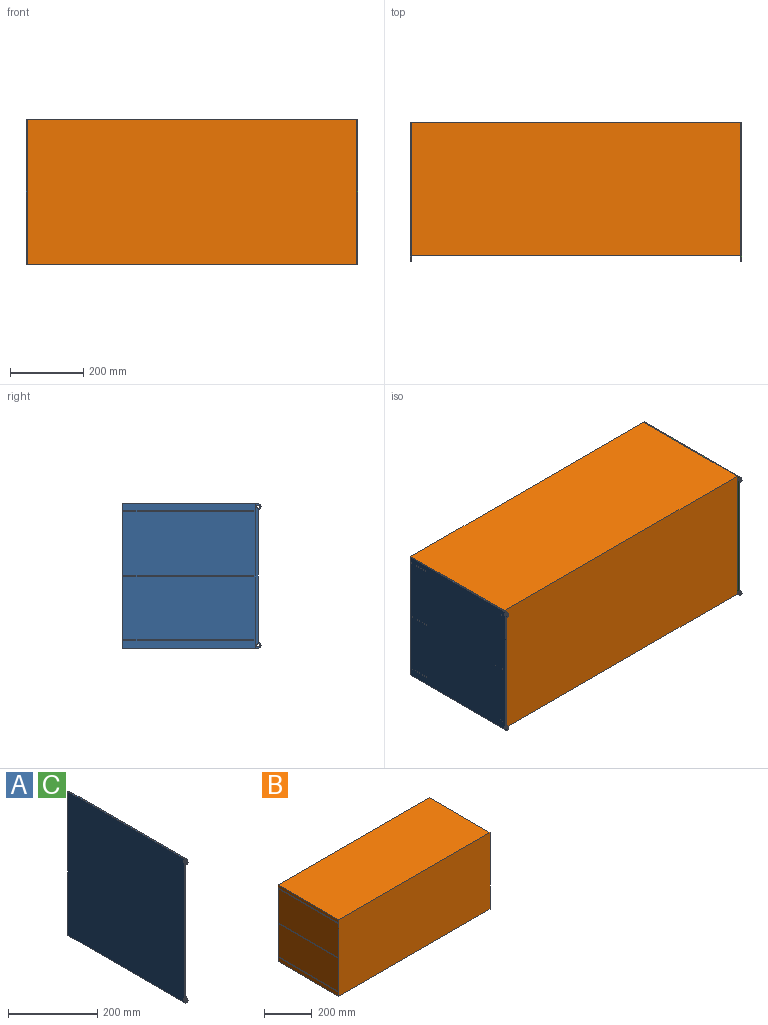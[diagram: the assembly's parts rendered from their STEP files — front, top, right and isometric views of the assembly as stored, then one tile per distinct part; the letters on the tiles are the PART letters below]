
ASSEMBLY  parts=3 mates=2
PART A: 10 faces, bbox 3.2x377.4x394.5 mm
  f0: cylinder r=7.87mm len=15.75mm, axis (-1,0,0), area 78.5mm2, adj f1,f7,f8,f9
  f1: plane 362.99x3.18mm, normal (0,-1,0), area 1152.5mm2, adj f0,f2,f8,f9
  f2: cylinder r=7.87mm len=15.75mm, axis (-1,0,0), area 78.5mm2, adj f1,f3,f8,f9
  f3: plane 369.49x3.18mm, normal (0,0,-1), area 1173.1mm2, adj f2,f4,f8,f9
  f4: plane 394.49x3.18mm, normal (0,1,0), area 1252.5mm2, adj f3,f7,f8,f9
  f5: cylinder r=4mm len=8mm, axis (-1,0,0), area 79.8mm2, adj f8,f9
  f6: cylinder r=4mm len=8mm, axis (-1,0,0), area 79.8mm2, adj f8,f9
  f7: plane 369.49x3.18mm, normal (0,0,1), area 1173.1mm2, adj f0,f4,f8,f9
  f8: plane 394.49x377.37mm, normal (1,0,0), area 145854.9mm2, adj f0,f1,f2,f3,f4,f5,f6,f7
  f9: plane 394.49x377.37mm, normal (-1,0,0), area 145854.9mm2, adj f0,f1,f2,f3,f4,f5,f6,f7
PART B: 50 faces, bbox 900.1x362x394.5 mm
  f0: cylinder r=8.99mm len=12.7mm, axis (0,1,0), area 177.9mm2, adj f2,f9,f39,f47
  f1: cylinder r=8.99mm len=19.05mm, axis (0,1,0), area 266.8mm2, adj f3,f10,f21,f46
  f2: plane 120x12.7mm, normal (0,0,1), area 1524mm2, adj f0,f4,f39,f47
  f3: plane 120x19.05mm, normal (0,0,1), area 2286mm2, adj f1,f5,f21,f46
  f4: cylinder r=9.07mm len=12.7mm, axis (0,1,0), area 179.2mm2, adj f2,f6,f39,f47
  f5: cylinder r=9.07mm len=19.05mm, axis (0,1,0), area 268.8mm2, adj f3,f7,f21,f46
  f6: plane 13.79x12.7mm, normal (-1,0,0), area 175.1mm2, adj f4,f8,f39,f47
  f7: plane 19.05x13.79mm, normal (-1,0,0), area 262.7mm2, adj f5,f8,f21,f46
  f8: plane 381.08x355.6mm, normal (0,0,1), area 18268.5mm2, adj f6,f7,f21,f29,f39,f46,f47,f48
  f9: plane 13.85x12.7mm, normal (1,0,0), area 175.9mm2, adj f0,f37,f39,f47
  f10: plane 19.05x13.85mm, normal (1,0,0), area 263.8mm2, adj f1,f21,f37,f46
  f11: cylinder r=8.99mm len=12.7mm, axis (0,1,0), area 177.9mm2, adj f13,f19,f36,f44
  f12: cylinder r=8.99mm len=19.05mm, axis (0,1,0), area 266.8mm2, adj f14,f20,f22,f42
  f13: plane 120x12.7mm, normal (0,0,1), area 1524mm2, adj f11,f15,f36,f44
  f14: plane 120x19.05mm, normal (0,0,1), area 2286mm2, adj f12,f16,f22,f42
  f15: cylinder r=9.07mm len=12.7mm, axis (0,1,0), area 179.2mm2, adj f13,f35,f36,f44
  f16: cylinder r=9.07mm len=19.05mm, axis (0,1,0), area 268.8mm2, adj f14,f17,f22,f42
  f17: plane 19.05x13.79mm, normal (-1,0,0), area 262.7mm2, adj f16,f18,f22,f42
  f18: plane 381.08x355.6mm, normal (0,0,1), area 18268.5mm2, adj f17,f22,f29,f35,f36,f42,f43,f44
  f19: plane 13.85x12.7mm, normal (1,0,0), area 175.9mm2, adj f11,f33,f36,f44
  f20: plane 19.05x13.85mm, normal (1,0,0), area 263.8mm2, adj f12,f22,f33,f42
  f21: plane 900.11x175.83mm, normal (0,1,0), area 155168.3mm2, adj f1,f3,f5,f7,f8,f10,f24,f29
  f22: plane 900.11x171.1mm, normal (0,1,0), area 150908.4mm2, adj f12,f14,f16,f17,f18,f20,f24,f29
  f23: plane 900.11x21.22mm, normal (0,1,0), area 19100.1mm2, adj f24,f28,f29,f31
  f24: plane 394.49x361.95mm, normal (-1,0,0), area 139397.6mm2, adj f21,f22,f23,f25,f26,f27,f28,f30
  f25: plane 900.11x394.49mm, normal (0,-1,0), area 355083mm2, adj f24,f26,f28,f29
  f26: plane 900.11x361.95mm, normal (0,0,1), area 325795.7mm2, adj f24,f25,f27,f29
  f27: plane 900.11x16.81mm, normal (0,1,0), area 15128.5mm2, adj f24,f26,f29,f38
  f28: plane 900.11x361.95mm, normal (0,0,-1), area 325795.7mm2, adj f23,f24,f25,f29
  f29: plane 394.49x361.95mm, normal (1,0,0), area 139397.6mm2, adj f8,f18,f21,f22,f23,f25,f26,f27
  f30: plane 900.11x355.6mm, normal (0,0,-1), area 320080mm2, adj f22,f24,f29,f32
  f31: plane 900.11x355.6mm, normal (0,0,1), area 320080mm2, adj f23,f24,f29,f32
  f32: plane 900.11x3.18mm, normal (0,1,0), area 2857.9mm2, adj f24,f29,f30,f31
  f33: plane 380.98x355.6mm, normal (0,0,1), area 18265.5mm2, adj f19,f20,f22,f24,f36,f41,f42,f44
  f34: plane 900.11x355.6mm, normal (0,0,-1), area 320080mm2, adj f21,f24,f29,f36
  f35: plane 13.79x12.7mm, normal (-1,0,0), area 175.1mm2, adj f15,f18,f36,f44
  f36: plane 900.11x25.9mm, normal (0,1,0), area 5959.9mm2, adj f11,f13,f15,f18,f19,f24,f29,f33
  f37: plane 380.98x355.6mm, normal (0,0,1), area 18265.5mm2, adj f9,f10,f21,f24,f39,f45,f46,f47
  f38: plane 900.11x355.6mm, normal (0,0,-1), area 320080mm2, adj f24,f27,f29,f39
  f39: plane 900.11x25.9mm, normal (0,1,0), area 5959.9mm2, adj f0,f2,f4,f6,f8,f9,f24,f29
  f40: plane 862.01x323.85mm, normal (0,0,1), area 279162.7mm2, adj f41,f42,f43,f44
  f41: plane 323.85x152.05mm, normal (1,0,0), area 49241.8mm2, adj f33,f40,f42,f44
  f42: plane 862.01x152.05mm, normal (0,-1,0), area 127968.1mm2, adj f12,f14,f16,f17,f18,f20,f33,f40
  f43: plane 323.85x152.05mm, normal (-1,0,0), area 49241.8mm2, adj f18,f40,f42,f44
  f44: plane 862.01x152.05mm, normal (0,1,0), area 127968.1mm2, adj f11,f13,f15,f18,f19,f33,f35,f40
  f45: plane 323.85x156.78mm, normal (1,0,0), area 50774.5mm2, adj f37,f46,f47,f49
  f46: plane 862.01x156.78mm, normal (0,-1,0), area 132047.7mm2, adj f1,f3,f5,f7,f8,f10,f37,f45
  f47: plane 862.01x156.78mm, normal (0,1,0), area 132047.7mm2, adj f0,f2,f4,f6,f8,f9,f37,f45
  f48: plane 323.85x156.78mm, normal (-1,0,0), area 50774.5mm2, adj f8,f46,f47,f49
  f49: plane 862.01x323.85mm, normal (0,0,1), area 279162.7mm2, adj f45,f46,f47,f48
PART C: same geometry as A
PLACE A t=(-3567.92,6150.12,-3330.9)mm
PLACE B t=(-3735.11,6150.12,-2845.23)mm
PLACE C t=(-2664.63,6150.12,-3330.9)mm
MATE fastened A.f8 <-> B.f24  axis (1,0,0) through (-3564.74,-2015.38,-399.89)mm
MATE fastened C.f9 <-> B.f29  axis (-1,0,0) through (-2664.63,-2015.38,-399.89)mm
